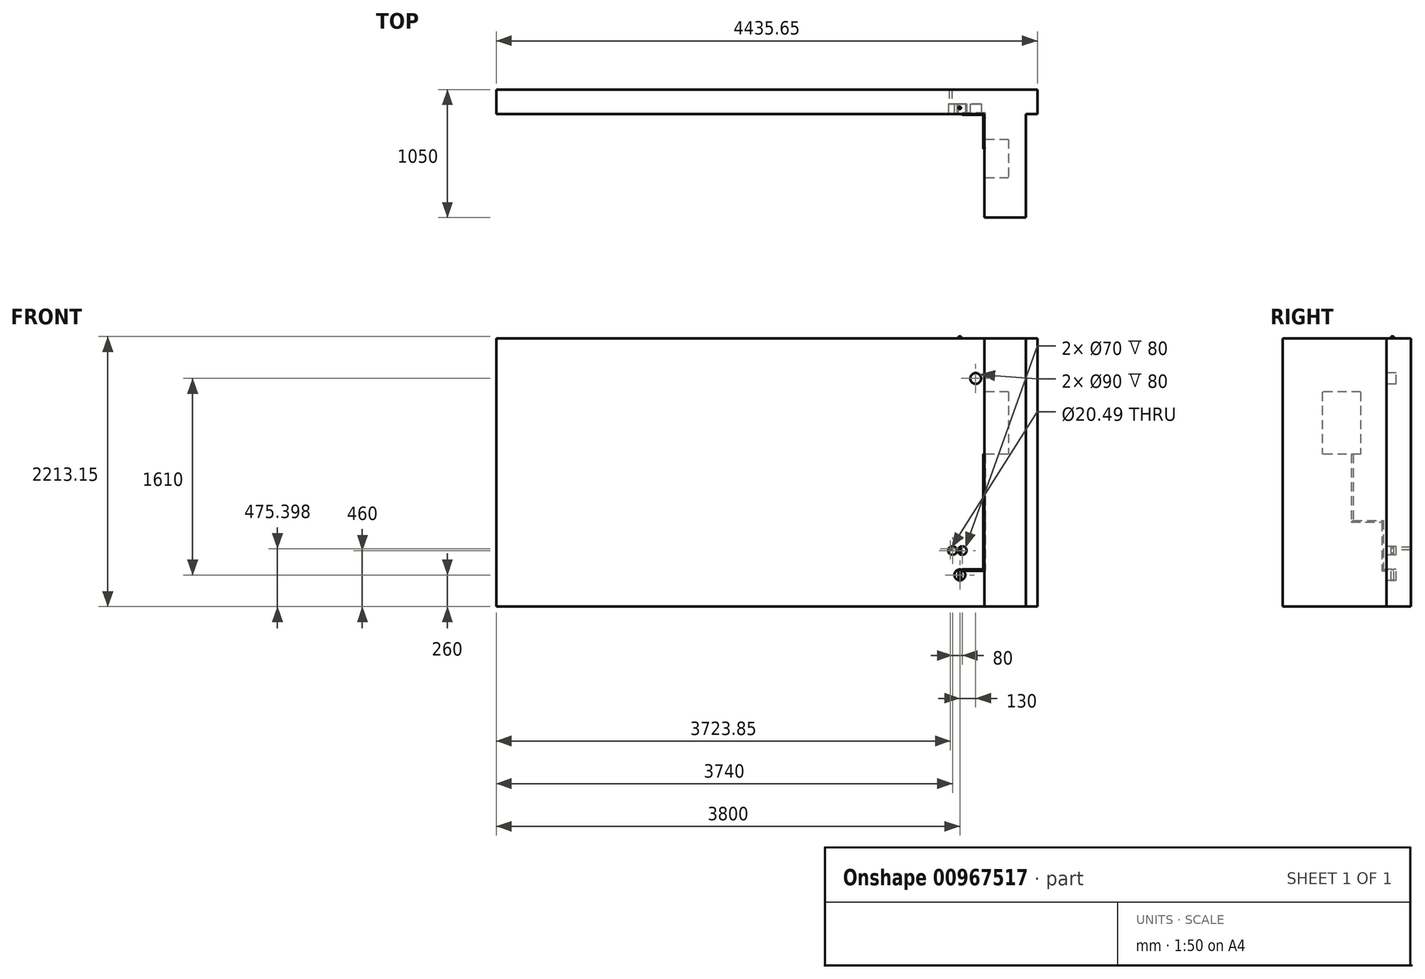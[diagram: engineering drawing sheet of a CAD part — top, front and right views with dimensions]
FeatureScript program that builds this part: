
annotation { "Feature Type Name" : "Feature", "Feature Type Description" : "" }
export const myFeature = defineFeature(function(context is Context, id is Id, definition is map)
    precondition{}
    {
        {
            var Q0;
            Q0=qCreatedBy(makeId("Top.planeOp"),FACE);
            var sketch = newSketch(context, id + "F0", { "sketchPlane" : qUnion([Q0])});
            skLineSegment(sketch, "E0", {"start": v(0, 0) * mm, "end": v(0, -850) * mm});
            skLineSegment(sketch, "E1", {"start": v(0, -850) * mm, "end": v(340, -850) * mm});
            skLineSegment(sketch, "E2", {"start": v(340, -850) * mm, "end": v(340, 0) * mm});
            skLineSegment(sketch, "E3", {"start": v(340, 0) * mm, "end": v(435.65, 0) * mm});
            skLineSegment(sketch, "E4", {"start": v(435.65, 0) * mm, "end": v(435.65, 200) * mm});
            skLineSegment(sketch, "E5", {"start": v(435.65, 200) * mm, "end": v(-4000, 200) * mm});
            skLineSegment(sketch, "E6", {"start": v(-4000, 200) * mm, "end": v(-4000, 0) * mm});
            skLineSegment(sketch, "E7", {"start": v(-4000, 0) * mm, "end": v(0, 0) * mm});
            skSolve(sketch);
        }
        {
            var Q0;
            Q0 = qSketchRegion(id + "F0", true);
            extrude(context, id + "F1", {"entities" : qUnion([Q0]), "depth" : 2200 * mm, "offsetDistance" : 25 * mm});
        }
        {
            var Q0;
            Q0=makeQuery(id+"F1.opExtrude","SWEPT_FACE",FACE,{"disambiguationData":[OSD([sQuery(id+"F0.wireOp",EDGE,"E0")])]});
            var sketch = newSketch(context, id + "F2", { "sketchPlane" : qUnion([Q0])});
            skLineSegment(sketch, "E8.bottom", {"start": v(210, 1760) * mm, "end": v(525, 1760) * mm});
            skLineSegment(sketch, "E8.top", {"start": v(210, 1250) * mm, "end": v(525, 1250) * mm});
            skLineSegment(sketch, "E8.left", {"start": v(210, 1760) * mm, "end": v(210, 1250) * mm});
            skLineSegment(sketch, "E8.right", {"start": v(525, 1760) * mm, "end": v(525, 1250) * mm});
            skSolve(sketch);
        }
        {
            var Q0;
            Q0 = qSketchRegion(id + "F2", true);
            extrude(context, id + "F3", {"entities" : qUnion([Q0]), "operationType" : NewBodyOperationType.REMOVE, "oppositeDirection" : true, "depth" : 200 * mm, "offsetDistance" : 25 * mm});
        }
        {
            var Q0;
            Q0=makeQuery(id+"F1.opExtrude","SWEPT_FACE",FACE,{"disambiguationData":[OSD([sQuery(id+"F0.wireOp",EDGE,"E0")])]});
            var sketch = newSketch(context, id + "F4", { "sketchPlane" : qUnion([Q0])});
            skLineSegment(sketch, "E9", {"start": v(0, 300) * mm, "end": v(30, 300) * mm});
            skLineSegment(sketch, "E10", {"start": v(30, 300) * mm, "end": v(30, 700) * mm});
            skLineSegment(sketch, "E11", {"start": v(30, 700) * mm, "end": v(280, 700) * mm});
            skLineSegment(sketch, "E12", {"start": v(280, 700) * mm, "end": v(280, 1250) * mm});
            skSolve(sketch);
        }
        {
            var Q0;
            Q0=makeQuery(id+"F1.opExtrude","SWEPT_FACE",FACE,{"disambiguationData":[OSD([sQuery(id+"F0.wireOp",EDGE,"E7")])]});
            var sketch = newSketch(context, id + "F5", { "sketchPlane" : qUnion([Q0])});
            skCircle(sketch, "E13", {"center": v(-200, 260) * mm, "radius": 45 * mm});
            skCircle(sketch, "E14", {"center": v(-70, 1870) * mm, "radius": 45 * mm});
            skCircle(sketch, "E15", {"center": v(-180, 460) * mm, "radius": 35 * mm});
            skCircle(sketch, "E16", {"center": v(-260, 460) * mm, "radius": 35 * mm});
            skSolve(sketch);
        }
        {
            var Q0;
            Q0 = qSketchRegion(id + "F5", true);
            extrude(context, id + "F6", {"entities" : qUnion([Q0]), "operationType" : NewBodyOperationType.REMOVE, "oppositeDirection" : true, "depth" : 80 * mm, "offsetDistance" : 25 * mm});
        }
        {
            var Q0;
            Q0=makeQuery(id+"F1.opExtrude","SWEPT_FACE",FACE,{"disambiguationData":[OSD([sQuery(id+"F0.wireOp",EDGE,"E7")])]});
            var sketch = newSketch(context, id + "F7", { "sketchPlane" : qUnion([Q0])});
            skLineSegment(sketch, "E17", {"start": v(-179.38, 300) * mm, "end": v(0, 300) * mm});
            skLineSegment(sketch, "E18", {"start": v(-249.94, 426.48) * mm, "end": v(-212.93, 303.1) * mm});
            skLineSegment(sketch, "E19", {"start": v(-200, 215) * mm, "end": v(-200, 0) * mm});
            skLineSegment(sketch, "E20", {"start": v(-200, 305) * mm, "end": v(-200, 2518.15) * mm});
            skLineSegment(sketch, "E21", {"start": v(-177.28, 494.9) * mm, "end": v(-73.5, 1825.14) * mm});
            skSolve(sketch);
        }
        {
            var Q0;
            Q0=qCreatedBy(makeId("Top.planeOp"),FACE);
            var sketch = newSketch(context, id + "F8", { "sketchPlane" : qUnion([Q0])});
            skCircle(sketch, "E22", {"center": v(-200, 50) * mm, "radius": 10 * mm});
            skSolve(sketch);
        }
        {
            var Q0;
            Q0 = qSketchRegion(id + "F8", true);
            var Q1;
            Q1=sQuery(id+"F7.wireOp",EDGE,"E19");
            sweep(context, id + "F9", {"profiles" : qUnion([Q0]), "path" : qUnion([Q1])});
        }
        {
            var Q0;
            Q0 = qSketchRegion(id + "F8", true);
            var Q1;
            Q1=sQuery(id+"F7.wireOp",EDGE,"E20");
            sweep(context, id + "F10", {"operationType" : NewBodyOperationType.ADD, "profiles" : qUnion([Q0]), "path" : qUnion([Q1])});
        }
        {
            var Q0;
            Q0=qCreatedBy(makeId("Right.planeOp"),FACE);
            var sketch = newSketch(context, id + "F11", { "sketchPlane" : qUnion([Q0])});
            skCircle(sketch, "E23", {"center": v(0, 300) * mm, "radius": 7.5 * mm});
            skSolve(sketch);
        }
        {
            var Q0;
            Q0 = qSketchRegion(id + "F11", true);
            var Q1;
            Q1=sQuery(id+"F7.wireOp",EDGE,"E17");
            var Q2;
            Q2=sQuery(id+"F4.wireOp",EDGE,"E9");
            var Q3;
            Q3=sQuery(id+"F4.wireOp",EDGE,"E10");
            var Q4;
            Q4=sQuery(id+"F4.wireOp",EDGE,"E11");
            var Q5;
            Q5=sQuery(id+"F4.wireOp",EDGE,"E12");
            sweep(context, id + "F12", {"profiles" : qUnion([Q0]), "path" : qUnion([Q1, Q2, Q3, Q4, Q5])});
        }
        {
            var Q0;
            Q0=makeQuery(id+"F6.boolean.opBoolean","COPY",FACE,{"derivedFrom":makeQuery(id+"F6.opExtrude","CAP_FACE",FACE,{"disambiguationData":[OSD([sQuery(id+"F5.wireOp",EDGE,"E16")])],"isStart":false})});
            var sketch = newSketch(context, id + "F13", { "sketchPlane" : qUnion([Q0])});
            skCircle(sketch, "E24", {"center": v(-276.15, 475.4) * mm, "radius": 10.24 * mm});
            skSolve(sketch);
        }
        {
            var Q0;
            Q0 = qSketchRegion(id + "F13", true);
            extrude(context, id + "F14", {"entities" : qUnion([Q0]), "operationType" : NewBodyOperationType.REMOVE, "endBound" : BoundingType.THROUGH_ALL, "oppositeDirection" : true, "depth" : 25 * mm, "offsetDistance" : 25 * mm});
        }
    });
